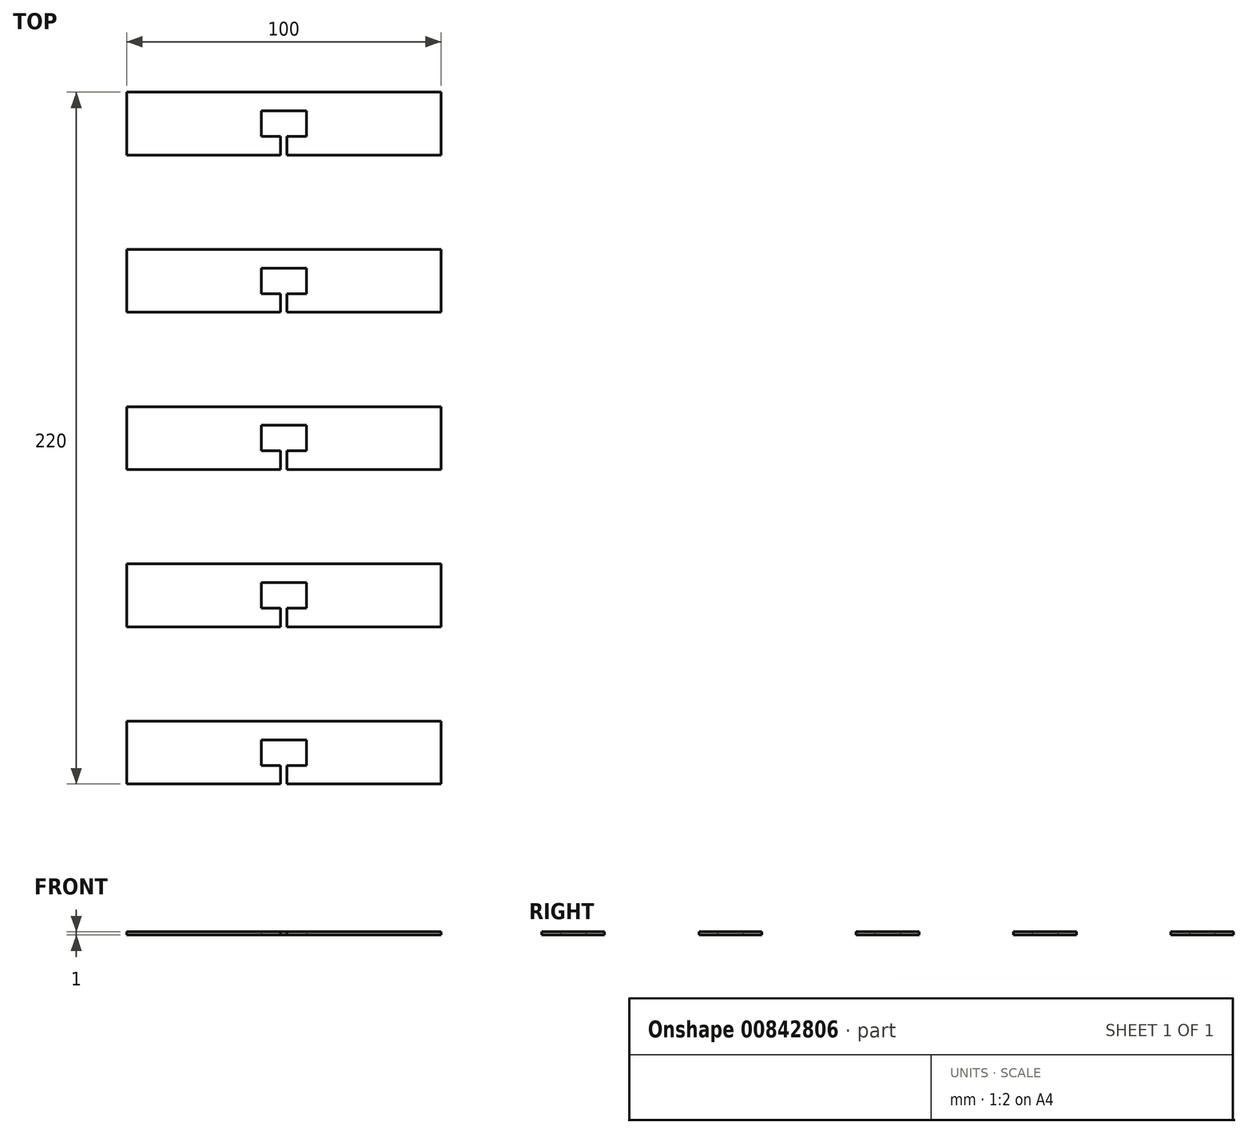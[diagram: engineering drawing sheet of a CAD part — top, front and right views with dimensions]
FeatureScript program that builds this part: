
annotation { "Feature Type Name" : "Feature", "Feature Type Description" : "" }
export const myFeature = defineFeature(function(context is Context, id is Id, definition is map)
    precondition{}
    {
        {
            var Q0;
            Q0=qCreatedBy(makeId("Top.planeOp"),FACE);
            var sketch = newSketch(context, id + "F0", { "sketchPlane" : qUnion([Q0])});
            skLineSegment(sketch, "E0", {"start": v(0, 10) * mm, "end": v(50, 10) * mm});
            skLineSegment(sketch, "E1", {"start": v(50, 10) * mm, "end": v(50, 0) * mm});
            skLineSegment(sketch, "E2", {"start": v(0, 4.06) * mm, "end": v(7.15, 4.06) * mm});
            skLineSegment(sketch, "E3", {"start": v(7.15, 4.06) * mm, "end": v(7.15, 0) * mm});
            skLineSegment(sketch, "E4.MirrorCS", {"start": v(0, 10) * mm, "end": v(-50, 10) * mm});
            skLineSegment(sketch, "E5.MirrorCS", {"start": v(-50, 10) * mm, "end": v(-50, 0) * mm});
            skLineSegment(sketch, "E6.MirrorCS", {"start": v(0, 4.06) * mm, "end": v(-7.15, 4.06) * mm});
            skLineSegment(sketch, "E7.MirrorCS", {"start": v(-7.15, 4.06) * mm, "end": v(-7.15, 0) * mm});
            skLineSegment(sketch, "E8.MirrorCS", {"start": v(-1, -4.06) * mm, "end": v(-7.15, -4.06) * mm});
            skLineSegment(sketch, "E9.MirrorCS", {"start": v(1, -4.06) * mm, "end": v(7.15, -4.06) * mm});
            skLineSegment(sketch, "E10.MirrorCS", {"start": v(1, -10) * mm, "end": v(50, -10) * mm});
            skLineSegment(sketch, "E11.MirrorCS", {"start": v(-1, -10) * mm, "end": v(-50, -10) * mm});
            skLineSegment(sketch, "E12.MirrorCS", {"start": v(-50, -10) * mm, "end": v(-50, 0) * mm});
            skLineSegment(sketch, "E13.MirrorCS", {"start": v(50, -10) * mm, "end": v(50, 0) * mm});
            skLineSegment(sketch, "E14.MirrorCS", {"start": v(-7.15, -4.06) * mm, "end": v(-7.15, 0) * mm});
            skLineSegment(sketch, "E15.MirrorCS", {"start": v(7.15, -4.06) * mm, "end": v(7.15, 0) * mm});
            skLineSegment(sketch, "E16", {"start": v(-1, -4.06) * mm, "end": v(-1, -10) * mm});
            skLineSegment(sketch, "E17.MirrorCS", {"start": v(1, -4.06) * mm, "end": v(1, -10) * mm});
            skPoint(sketch, "E18.orphan", {"position": v(0, -4.06) * mm});
            skPoint(sketch, "E19.orphan", {"position": v(0, -10) * mm});
            skLineSegment(sketch, "E20.0.1.0", {"start": v(50, 60) * mm, "end": v(50, 50) * mm});
            skLineSegment(sketch, "E20.0.1.1", {"start": v(-50, 60) * mm, "end": v(-50, 50) * mm});
            skLineSegment(sketch, "E20.0.1.2", {"start": v(0, 60) * mm, "end": v(50, 60) * mm});
            skPoint(sketch, "E20.0.1.3", {"position": v(0, 45.94) * mm});
            skLineSegment(sketch, "E20.0.1.4", {"start": v(-50, 40) * mm, "end": v(-50, 50) * mm});
            skLineSegment(sketch, "E20.0.1.5", {"start": v(0, 54.06) * mm, "end": v(-7.15, 54.06) * mm});
            skLineSegment(sketch, "E20.0.1.6", {"start": v(0, 60) * mm, "end": v(-50, 60) * mm});
            skLineSegment(sketch, "E20.0.1.7", {"start": v(0, 54.06) * mm, "end": v(7.15, 54.06) * mm});
            skLineSegment(sketch, "E20.0.1.8", {"start": v(-1, 45.94) * mm, "end": v(-7.15, 45.94) * mm});
            skLineSegment(sketch, "E20.0.1.9", {"start": v(1, 40) * mm, "end": v(50, 40) * mm});
            skLineSegment(sketch, "E20.0.1.10", {"start": v(1, 45.94) * mm, "end": v(7.15, 45.94) * mm});
            skLineSegment(sketch, "E20.0.1.11", {"start": v(-1, 40) * mm, "end": v(-50, 40) * mm});
            skPoint(sketch, "E20.0.1.12", {"position": v(0, 40) * mm});
            skLineSegment(sketch, "E20.0.1.13", {"start": v(50, 40) * mm, "end": v(50, 50) * mm});
            skPoint(sketch, "E20.0.1.14", {"position": v(0, 40) * mm});
            skPoint(sketch, "E20.0.1.15", {"position": v(0, 45.94) * mm});
            skLineSegment(sketch, "E20.0.1.16", {"start": v(-1, 45.94) * mm, "end": v(-1, 40) * mm});
            skLineSegment(sketch, "E20.0.1.17", {"start": v(7.15, 45.94) * mm, "end": v(7.15, 50) * mm});
            skLineSegment(sketch, "E20.0.1.18", {"start": v(-7.15, 54.06) * mm, "end": v(-7.15, 50) * mm});
            skLineSegment(sketch, "E20.0.1.19", {"start": v(1, 45.94) * mm, "end": v(1, 40) * mm});
            skLineSegment(sketch, "E20.0.1.20", {"start": v(7.15, 54.06) * mm, "end": v(7.15, 50) * mm});
            skLineSegment(sketch, "E20.0.1.21", {"start": v(-7.15, 45.94) * mm, "end": v(-7.15, 50) * mm});
            skLineSegment(sketch, "E20.0.2.0", {"start": v(50, 110) * mm, "end": v(50, 100) * mm});
            skLineSegment(sketch, "E20.0.2.1", {"start": v(-50, 110) * mm, "end": v(-50, 100) * mm});
            skLineSegment(sketch, "E20.0.2.2", {"start": v(0, 110) * mm, "end": v(50, 110) * mm});
            skPoint(sketch, "E20.0.2.3", {"position": v(0, 95.94) * mm});
            skLineSegment(sketch, "E20.0.2.4", {"start": v(-50, 90) * mm, "end": v(-50, 100) * mm});
            skLineSegment(sketch, "E20.0.2.5", {"start": v(0, 104.06) * mm, "end": v(-7.15, 104.06) * mm});
            skLineSegment(sketch, "E20.0.2.6", {"start": v(0, 110) * mm, "end": v(-50, 110) * mm});
            skLineSegment(sketch, "E20.0.2.7", {"start": v(0, 104.06) * mm, "end": v(7.15, 104.06) * mm});
            skLineSegment(sketch, "E20.0.2.8", {"start": v(-1, 95.94) * mm, "end": v(-7.15, 95.94) * mm});
            skLineSegment(sketch, "E20.0.2.9", {"start": v(1, 90) * mm, "end": v(50, 90) * mm});
            skLineSegment(sketch, "E20.0.2.10", {"start": v(1, 95.94) * mm, "end": v(7.15, 95.94) * mm});
            skLineSegment(sketch, "E20.0.2.11", {"start": v(-1, 90) * mm, "end": v(-50, 90) * mm});
            skPoint(sketch, "E20.0.2.12", {"position": v(0, 90) * mm});
            skLineSegment(sketch, "E20.0.2.13", {"start": v(50, 90) * mm, "end": v(50, 100) * mm});
            skPoint(sketch, "E20.0.2.14", {"position": v(0, 90) * mm});
            skPoint(sketch, "E20.0.2.15", {"position": v(0, 95.94) * mm});
            skLineSegment(sketch, "E20.0.2.16", {"start": v(-1, 95.94) * mm, "end": v(-1, 90) * mm});
            skLineSegment(sketch, "E20.0.2.17", {"start": v(7.15, 95.94) * mm, "end": v(7.15, 100) * mm});
            skLineSegment(sketch, "E20.0.2.18", {"start": v(-7.15, 104.06) * mm, "end": v(-7.15, 100) * mm});
            skLineSegment(sketch, "E20.0.2.19", {"start": v(1, 95.94) * mm, "end": v(1, 90) * mm});
            skLineSegment(sketch, "E20.0.2.20", {"start": v(7.15, 104.06) * mm, "end": v(7.15, 100) * mm});
            skLineSegment(sketch, "E20.0.2.21", {"start": v(-7.15, 95.94) * mm, "end": v(-7.15, 100) * mm});
            skLineSegment(sketch, "E20.0.3.0", {"start": v(50, 160) * mm, "end": v(50, 150) * mm});
            skLineSegment(sketch, "E20.0.3.1", {"start": v(-50, 160) * mm, "end": v(-50, 150) * mm});
            skLineSegment(sketch, "E20.0.3.2", {"start": v(0, 160) * mm, "end": v(50, 160) * mm});
            skPoint(sketch, "E20.0.3.3", {"position": v(0, 145.94) * mm});
            skLineSegment(sketch, "E20.0.3.4", {"start": v(-50, 140) * mm, "end": v(-50, 150) * mm});
            skLineSegment(sketch, "E20.0.3.5", {"start": v(0, 154.06) * mm, "end": v(-7.15, 154.06) * mm});
            skLineSegment(sketch, "E20.0.3.6", {"start": v(0, 160) * mm, "end": v(-50, 160) * mm});
            skLineSegment(sketch, "E20.0.3.7", {"start": v(0, 154.06) * mm, "end": v(7.15, 154.06) * mm});
            skLineSegment(sketch, "E20.0.3.8", {"start": v(-1, 145.94) * mm, "end": v(-7.15, 145.94) * mm});
            skLineSegment(sketch, "E20.0.3.9", {"start": v(1, 140) * mm, "end": v(50, 140) * mm});
            skLineSegment(sketch, "E20.0.3.10", {"start": v(1, 145.94) * mm, "end": v(7.15, 145.94) * mm});
            skLineSegment(sketch, "E20.0.3.11", {"start": v(-1, 140) * mm, "end": v(-50, 140) * mm});
            skPoint(sketch, "E20.0.3.12", {"position": v(0, 140) * mm});
            skLineSegment(sketch, "E20.0.3.13", {"start": v(50, 140) * mm, "end": v(50, 150) * mm});
            skPoint(sketch, "E20.0.3.14", {"position": v(0, 140) * mm});
            skPoint(sketch, "E20.0.3.15", {"position": v(0, 145.94) * mm});
            skLineSegment(sketch, "E20.0.3.16", {"start": v(-1, 145.94) * mm, "end": v(-1, 140) * mm});
            skLineSegment(sketch, "E20.0.3.17", {"start": v(7.15, 145.94) * mm, "end": v(7.15, 150) * mm});
            skLineSegment(sketch, "E20.0.3.18", {"start": v(-7.15, 154.06) * mm, "end": v(-7.15, 150) * mm});
            skLineSegment(sketch, "E20.0.3.19", {"start": v(1, 145.94) * mm, "end": v(1, 140) * mm});
            skLineSegment(sketch, "E20.0.3.20", {"start": v(7.15, 154.06) * mm, "end": v(7.15, 150) * mm});
            skLineSegment(sketch, "E20.0.3.21", {"start": v(-7.15, 145.94) * mm, "end": v(-7.15, 150) * mm});
            skLineSegment(sketch, "E20.0.4.0", {"start": v(50, 210) * mm, "end": v(50, 200) * mm});
            skLineSegment(sketch, "E20.0.4.1", {"start": v(-50, 210) * mm, "end": v(-50, 200) * mm});
            skLineSegment(sketch, "E20.0.4.2", {"start": v(0, 210) * mm, "end": v(50, 210) * mm});
            skPoint(sketch, "E20.0.4.3", {"position": v(0, 195.94) * mm});
            skLineSegment(sketch, "E20.0.4.4", {"start": v(-50, 190) * mm, "end": v(-50, 200) * mm});
            skLineSegment(sketch, "E20.0.4.5", {"start": v(0, 204.06) * mm, "end": v(-7.15, 204.06) * mm});
            skLineSegment(sketch, "E20.0.4.6", {"start": v(0, 210) * mm, "end": v(-50, 210) * mm});
            skLineSegment(sketch, "E20.0.4.7", {"start": v(0, 204.06) * mm, "end": v(7.15, 204.06) * mm});
            skLineSegment(sketch, "E20.0.4.8", {"start": v(-1, 195.94) * mm, "end": v(-7.15, 195.94) * mm});
            skLineSegment(sketch, "E20.0.4.9", {"start": v(1, 190) * mm, "end": v(50, 190) * mm});
            skLineSegment(sketch, "E20.0.4.10", {"start": v(1, 195.94) * mm, "end": v(7.15, 195.94) * mm});
            skLineSegment(sketch, "E20.0.4.11", {"start": v(-1, 190) * mm, "end": v(-50, 190) * mm});
            skPoint(sketch, "E20.0.4.12", {"position": v(0, 190) * mm});
            skLineSegment(sketch, "E20.0.4.13", {"start": v(50, 190) * mm, "end": v(50, 200) * mm});
            skPoint(sketch, "E20.0.4.14", {"position": v(0, 190) * mm});
            skPoint(sketch, "E20.0.4.15", {"position": v(0, 195.94) * mm});
            skLineSegment(sketch, "E20.0.4.16", {"start": v(-1, 195.94) * mm, "end": v(-1, 190) * mm});
            skLineSegment(sketch, "E20.0.4.17", {"start": v(7.15, 195.94) * mm, "end": v(7.15, 200) * mm});
            skLineSegment(sketch, "E20.0.4.18", {"start": v(-7.15, 204.06) * mm, "end": v(-7.15, 200) * mm});
            skLineSegment(sketch, "E20.0.4.19", {"start": v(1, 195.94) * mm, "end": v(1, 190) * mm});
            skLineSegment(sketch, "E20.0.4.20", {"start": v(7.15, 204.06) * mm, "end": v(7.15, 200) * mm});
            skLineSegment(sketch, "E20.0.4.21", {"start": v(-7.15, 195.94) * mm, "end": v(-7.15, 200) * mm});
            skLineSegment(sketch, "E20.direction1", {"start": v(-50, -10) * mm, "end": v(-25, -10) * mm, "construction": true});
            skLineSegment(sketch, "E20.direction2", {"start": v(-50, -10) * mm, "end": v(-50, 40) * mm, "construction": true});
            skSolve(sketch);
        }
        {
            var Q0;
            Q0 = qSketchRegion(id + "F0", true);
            extrude(context, id + "F1", {"entities" : qUnion([Q0]), "depth" : 1 * mm, "offsetDistance" : 25 * mm});
        }
    });
